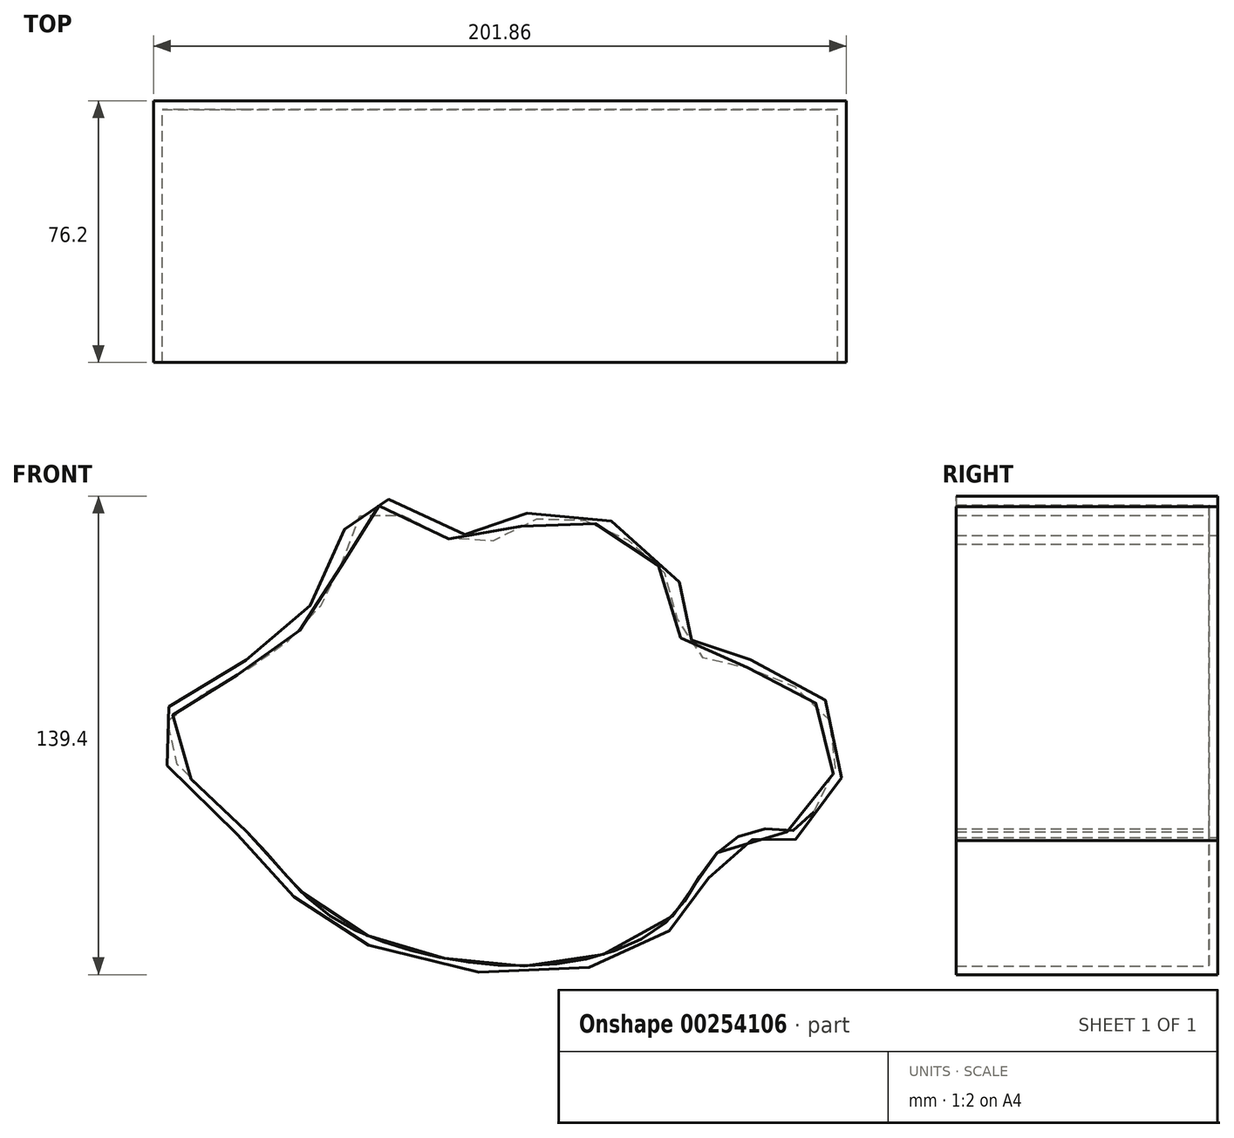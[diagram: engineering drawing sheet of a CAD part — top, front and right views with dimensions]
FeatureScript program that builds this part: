
annotation { "Feature Type Name" : "Feature", "Feature Type Description" : "" }
export const myFeature = defineFeature(function(context is Context, id is Id, definition is map)
    precondition{}
    {
        {
            var Q0;
            Q0=qCreatedBy(makeId("Front.planeOp"),FACE);
            var sketch = newSketch(context, id + "F0", { "sketchPlane" : qUnion([Q0])});
            skPoint(sketch, "E0.visualSharp", {"position": v(-89.67, 71.05) * mm});
            skPoint(sketch, "E1.visualSharp", {"position": v(62.73, 71.05) * mm});
            skPoint(sketch, "E2.visualSharp", {"position": v(-89.67, -30.55) * mm});
            skPoint(sketch, "E3.visualSharp", {"position": v(62.73, -30.55) * mm});
            skFitSpline(sketch, "E4", {"points": [v(41.79, 52.34) * mm, v(62.73, 45.65) * mm, v(86.76, 22.23) * mm, v(72.29, -5.53) * mm, v(62.73, -5.15) * mm, v(49.6, -12.96) * mm, v(37.33, -30.55) * mm, v(-3.96, -45.03) * mm, v(-64.27, -30.55) * mm, v(-89.67, -5.15) * mm, v(-115.02, 25.36) * mm, v(-89.67, 45.65) * mm, v(-64.27, 71.05) * mm, v(-52.06, 94.18) * mm, v(-22.73, 82.84) * mm, v(0, 91.06) * mm, v(37.33, 71.05) * mm, v(41.79, 52.34) * mm]});
            skSolve(sketch);
        }
        {
            var Q0;
            Q0=makeQuery(id+"F0.imprint","IMPRINT",FACE,{"disambiguationData":[TD([[makeQuery(id+"F0.imprint","IMPRINT",EDGE,{"derivedFrom":sQuery(id+"F0.wireOp",EDGE,"E4")}),-1.0]])]});
            extrude(context, id + "F1", {"entities" : qUnion([Q0]), "depth" : 76.2 * mm});
        }
        {
            var Q0;
            Q0=makeQuery(id+"F1.opExtrude","CAP_FACE",FACE,{"disambiguationData":[OSD([sQuery(id+"F0.wireOp",EDGE,"E4")])],"isStart":false});
            shell(context, id + "F2", {"entities" : qUnion([Q0]), "thickness" : 2.54 * mm});
        }
    });
